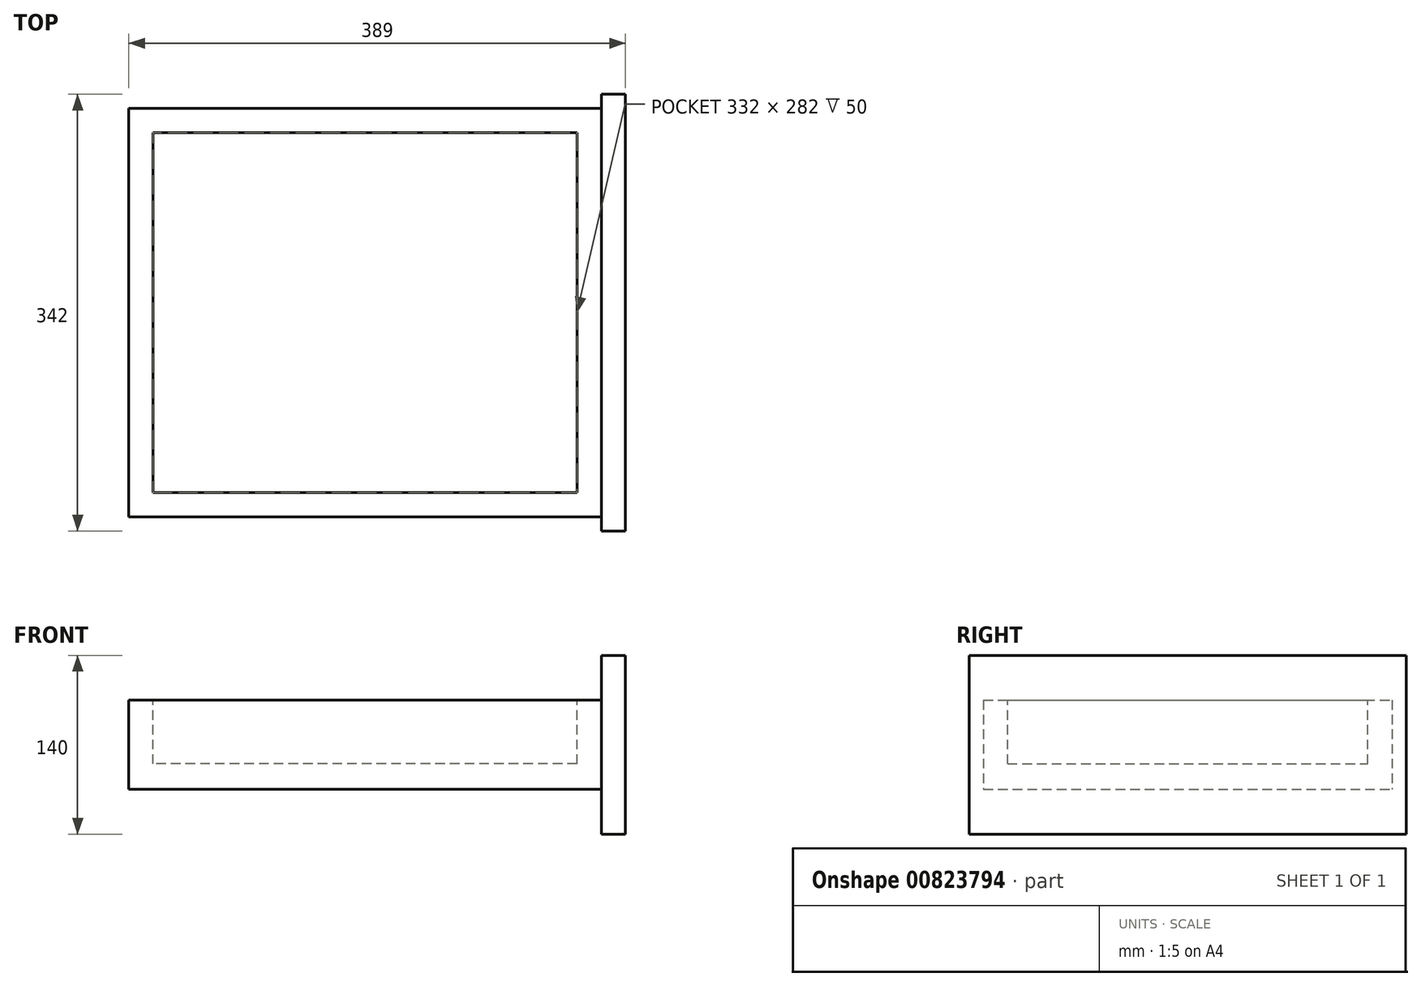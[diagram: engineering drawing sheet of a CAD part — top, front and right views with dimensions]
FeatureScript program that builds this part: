
annotation { "Feature Type Name" : "Feature", "Feature Type Description" : "" }
export const myFeature = defineFeature(function(context is Context, id is Id, definition is map)
    precondition{}
    {
        {
            var Q0;
            Q0=qCreatedBy(makeId("Top.planeOp"),FACE);
            var sketch = newSketch(context, id + "F0", { "sketchPlane" : qUnion([Q0])});
            skLineSegment(sketch, "E0.bottom", {"start": v(185, -160) * mm, "end": v(-185, -160) * mm});
            skLineSegment(sketch, "E0.top", {"start": v(185, 160) * mm, "end": v(-185, 160) * mm});
            skLineSegment(sketch, "E0.left", {"start": v(185, -160) * mm, "end": v(185, 160) * mm});
            skLineSegment(sketch, "E0.right", {"start": v(-185, -160) * mm, "end": v(-185, 160) * mm});
            skPoint(sketch, "E0.middle", {"position": v(0, 0) * mm});
            skSolve(sketch);
        }
        {
            var Q0;
            Q0=makeQuery(id+"F0.imprint","IMPRINT",FACE,{"disambiguationData":[TD([[makeQuery(id+"F0.imprint","IMPRINT",EDGE,{"derivedFrom":sQuery(id+"F0.wireOp",EDGE,"E0.bottom")}),-1.0]])]});
            extrude(context, id + "F1", {"entities" : qUnion([Q0]), "depth" : 70 * mm, "offsetDistance" : 25 * mm});
        }
        {
            var Q0;
            Q0=makeQuery(id+"F1.opExtrude","CAP_FACE",FACE,{"disambiguationData":[OSD([sQuery(id+"F0.wireOp",EDGE,"E0.bottom"),sQuery(id+"F0.wireOp",EDGE,"E0.top"),sQuery(id+"F0.wireOp",EDGE,"E0.left"),sQuery(id+"F0.wireOp",EDGE,"E0.right")])],"isStart":false});
            var sketch = newSketch(context, id + "F2", { "sketchPlane" : qUnion([Q0])});
            skLineSegment(sketch, "E1.bottom", {"start": v(166, -141) * mm, "end": v(-166, -141) * mm});
            skLineSegment(sketch, "E1.top", {"start": v(166, 141) * mm, "end": v(-166, 141) * mm});
            skLineSegment(sketch, "E1.left", {"start": v(166, -141) * mm, "end": v(166, 141) * mm});
            skLineSegment(sketch, "E1.right", {"start": v(-166, -141) * mm, "end": v(-166, 141) * mm});
            skPoint(sketch, "E1.middle", {"position": v(0, 0) * mm});
            skSolve(sketch);
        }
        {
            var Q0;
            Q0=makeQuery(id+"F2.imprint","IMPRINT",FACE,{"disambiguationData":[TD([[makeQuery(id+"F2.imprint","IMPRINT",EDGE,{"derivedFrom":sQuery(id+"F2.wireOp",EDGE,"E1.bottom")}),-1.0]])]});
            extrude(context, id + "F3", {"entities" : qUnion([Q0]), "operationType" : NewBodyOperationType.REMOVE, "oppositeDirection" : true, "depth" : 25 * mm, "offsetDistance" : 25 * mm});
        }
        {
            var Q0;
            Q0=makeQuery(id+"F3.boolean.opBoolean","COPY",FACE,{"derivedFrom":makeQuery(id+"F3.opExtrude","CAP_FACE",FACE,{"disambiguationData":[OSD([sQuery(id+"F2.wireOp",EDGE,"E1.bottom"),sQuery(id+"F2.wireOp",EDGE,"E1.top"),sQuery(id+"F2.wireOp",EDGE,"E1.left"),sQuery(id+"F2.wireOp",EDGE,"E1.right")])],"isStart":false})});
            extrude(context, id + "F4", {"entities" : qUnion([Q0]), "operationType" : NewBodyOperationType.ADD, "oppositeDirection" : true, "depth" : 11 * mm, "offsetDistance" : 25 * mm});
        }
        {
            var Q0;
            Q0=makeQuery(id+"F3.boolean.opBoolean","COPY",FACE,{"derivedFrom":makeQuery(id+"F3.opExtrude","CAP_FACE",FACE,{"disambiguationData":[OSD([sQuery(id+"F2.wireOp",EDGE,"E1.bottom"),sQuery(id+"F2.wireOp",EDGE,"E1.top"),sQuery(id+"F2.wireOp",EDGE,"E1.left"),sQuery(id+"F2.wireOp",EDGE,"E1.right")])],"isStart":false})});
            extrude(context, id + "F5", {"entities" : qUnion([Q0]), "operationType" : NewBodyOperationType.REMOVE, "oppositeDirection" : true, "depth" : 25 * mm, "offsetDistance" : 25 * mm});
        }
        {
            var Q0;
            Q0=makeQuery(id+"F1.opExtrude","SWEPT_FACE",FACE,{"disambiguationData":[OSD([sQuery(id+"F0.wireOp",EDGE,"E0.left")])]});
            var sketch = newSketch(context, id + "F6", { "sketchPlane" : qUnion([Q0])});
            skLineSegment(sketch, "E2.bottom", {"start": v(-171, -35) * mm, "end": v(171, -35) * mm});
            skLineSegment(sketch, "E2.top", {"start": v(-171, 105) * mm, "end": v(171, 105) * mm});
            skLineSegment(sketch, "E2.left", {"start": v(-171, -35) * mm, "end": v(-171, 105) * mm});
            skLineSegment(sketch, "E2.right", {"start": v(171, -35) * mm, "end": v(171, 105) * mm});
            skPoint(sketch, "E2.middle", {"position": v(0, 35) * mm});
            skPoint(sketch, "E2.middle.positionSnap0", {"position": v(-160, 35) * mm});
            skPoint(sketch, "E2.centerSnap0", {"position": v(-160, 35) * mm});
            skSolve(sketch);
        }
        {
            var Q0;
            Q0=makeQuery(id+"F6.imprint","IMPRINT",FACE,{"disambiguationData":[TD([[makeQuery(id+"F6.imprint","IMPRINT",EDGE,{"derivedFrom":sQuery(id+"F6.wireOp",EDGE,"E2.bottom")}),1.0]])]});
            var Q1;
            {var subQ0=sQuery(id+"F0.wireOp",EDGE,"E0.left");Q1=makeQuery(id+"F6.imprint","IMPRINT",FACE,{"disambiguationData":[TD([[makeQuery(id+"F6.imprint","IMPRINT",EDGE,{"derivedFrom":makeQuery(id+"F1.opExtrude","CAP_EDGE",EDGE,{"disambiguationData":[OSD([subQ0])],"isStart":true})}),1.0]])]});}
            extrude(context, id + "F7", {"entities" : qUnion([Q0, Q1]), "operationType" : NewBodyOperationType.ADD, "depth" : 19 * mm, "offsetDistance" : 25 * mm});
        }
    });
